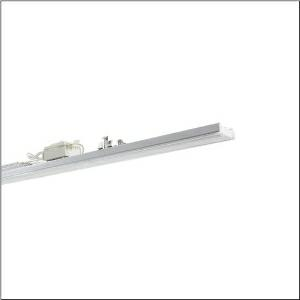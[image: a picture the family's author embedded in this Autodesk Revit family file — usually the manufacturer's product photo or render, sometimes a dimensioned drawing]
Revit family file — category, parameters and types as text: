
# Revit family: licross_11_recessed_ho_51te1ecn4cxs
name_source: partatom
category: Lighting Fixtures
units: mm (PartAtom-declared; Revit-internal decimal feet)

## family parameters
Cut with Voids When Loaded = No
Host = Face
Light Source = No
Part Type = Normal
Room Calculation Point = No
Round Connector Dimension = Use Diameter
Shared = No

## types (1)
- --- (1 x LED, 12420 lm, 66.5 W, 4000K)
    Apparent Load = 67 VA
    CIE Flux Codes = 85 95 99 100 100
    Color Rendering = 80
    Color Temperature = 4000K
    Default Elevation = 1800 mm
    Description = Licross 11 Recessed HO, luminaire insert, of sheet steel, galvanised, coil coated, white, length: 1.500mm, width: 66mm, height: 67mm, LED rated luminous flux: 12.420lm, light colour: 840, SDCM (Standard Deviation of Colour Matching)MacAdam ≤ 2 SDCM (initial), control gear: ON/OFF Multilumen, CLOi, with plug, 3-pole, with phase selection, mains connection: 220..240V, AC, 50/60Hz, start of lifetime: 67W, end of service life: 75W, internal wiring halogen-free, primary light control with lens, of plastic, primary optical cover: cover, of PMMA, light emission: direct distribution, primary light characteristic: symmetric, protection rating (complete): IP54, insulation class (complete): insulation class I (protective earthing), certification: CE, ENEC, VDE, UKCA, protection symbol: D if used in an environment with non-conductive dust loads with corresponding accessories, impact resistance: IK06, permissible ambient temperature for indoor applications: -35..+35°C, corresponds to IFS (International Featured Standards) requirements for safety and quality in the food industry, reducing of maximum allowable ambient temperature of 5°C with ceiling mounting, LABS conformity tested according to VDMA 24364:2018-05, The light source and the operating device comply with the requirements of the Ecodesign Regulation (EU) 2019/2020 and are replaceable in accordance with this regulation, packaging unit: 1 piece
    Height = 58 mm
    Lamp = 1 x LED
    Lamp Light Flux = 12420 lm
    Lamp Power = 66.5 W
    Lamp count = 1
    Length = 1500 mm
    Luminous efficacy = 187 lm/W
    Manufacturer = Siteco
    ModVariant = No
    Model = 51TE1ECN4CXS
    Mounting Place = Ceiling
    Mounting Type = Pendant
    Number of Poles = 1
    OnlyDefault = Yes
    Power Factor = 1
    Product Name = Licross 11 Recessed HO
    Product group = luminaire insert | ceiling pendant
    ProductGroupID = 901
    Protection Class = Protection class I
    Protection Degree = IP 54
    RLX_Detail_Level = 1
    RLX_Emergency_Light_Flux = 0 lm
    RLX_Emergency_Type = 0
    RLX_Emergency_Type_DB = No
    RlxData = <blob elided: 22717 chars, md5=aa414679>
    Socket = socket
    Standby Power = 0 W
    System Light Flux = 12420 lm
    System Power = 67 W
    Type Comments = factory setting: luminous flux: 100 % | (A | C | E) | 156 mA
    Type Image = l_1296930.jpg
    URL = http://relux.com
    VarID = @adj_000097
    Voltage = 0 V
    Weight = 0.00 kg
    Width = 66 mm

## geometry (parser evidence)
native form markers: Blend x4, Sweep x12
no freeform markers — native parametric forms only
